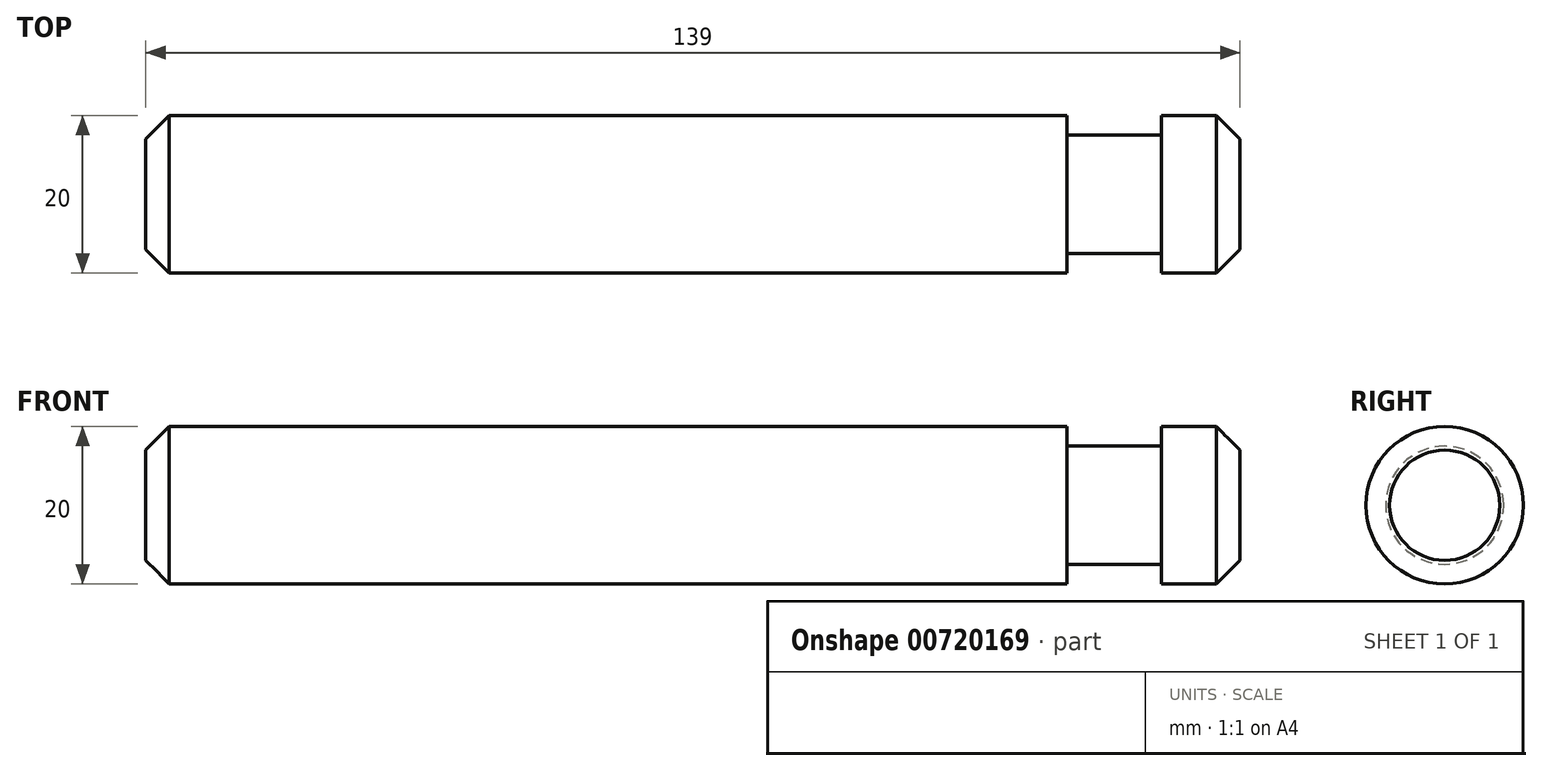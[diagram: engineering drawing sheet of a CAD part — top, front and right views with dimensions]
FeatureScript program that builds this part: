
annotation { "Feature Type Name" : "Feature", "Feature Type Description" : "" }
export const myFeature = defineFeature(function(context is Context, id is Id, definition is map)
    precondition{}
    {
        {
            var Q0;
            Q0=qCreatedBy(makeId("Front.planeOp"),FACE);
            var sketch = newSketch(context, id + "F0", { "sketchPlane" : qUnion([Q0])});
            skLineSegment(sketch, "E0", {"start": v(0, 0) * mm, "end": v(139, 0) * mm});
            skLineSegment(sketch, "E1", {"start": v(139, 0) * mm, "end": v(139, 10) * mm});
            skLineSegment(sketch, "E2", {"start": v(139, 10) * mm, "end": v(129, 10) * mm});
            skLineSegment(sketch, "E3", {"start": v(0, 10) * mm, "end": v(0, 0) * mm});
            skLineSegment(sketch, "E4.0", {"start": v(129, 7.5) * mm, "end": v(129, 10) * mm});
            skLineSegment(sketch, "E5.0", {"start": v(117, 7.5) * mm, "end": v(117, 10) * mm});
            skLineSegment(sketch, "E6.0", {"start": v(117, 7.5) * mm, "end": v(129, 7.5) * mm});
            skLineSegment(sketch, "E7.trimOffspring", {"start": v(117, 10) * mm, "end": v(0, 10) * mm});
            skSolve(sketch);
        }
        {
            var Q0;
            Q0=makeQuery(id+"F0.imprint","IMPRINT",FACE,{"disambiguationData":[TD([[makeQuery(id+"F0.imprint","IMPRINT",EDGE,{"derivedFrom":sQuery(id+"F0.wireOp",EDGE,"E0")}),1.0]])]});
            var Q1;
            Q1=sQuery(id+"F0.wireOp",EDGE,"E0");
            revolve(context, id + "F1", {"surfaceOperationType" : NewSurfaceOperationType.NEW, "entities" : qUnion([Q0]), "axis" : qUnion([Q1]), "revolveType" : RevolveType.FULL});
        }
        {
            var Q0;
            Q0=makeQuery(id+"F1.opRevolve","SWEPT_EDGE",EDGE,{"disambiguationData":[OSD([sQuery(id+"F0.wireOp",EDGE,"E1"),sQuery(id+"F0.wireOp",EDGE,"E2")])]});
            var Q1;
            Q1=makeQuery(id+"F1.opRevolve","SWEPT_EDGE",EDGE,{"disambiguationData":[OSD([sQuery(id+"F0.wireOp",EDGE,"E3"),sQuery(id+"F0.wireOp",EDGE,"E7.trimOffspring")])]});
            chamfer(context, id + "F2", {"entities" : qUnion([Q0, Q1]), "width" : 3 * mm, "tangentPropagation" : true});
        }
    });
